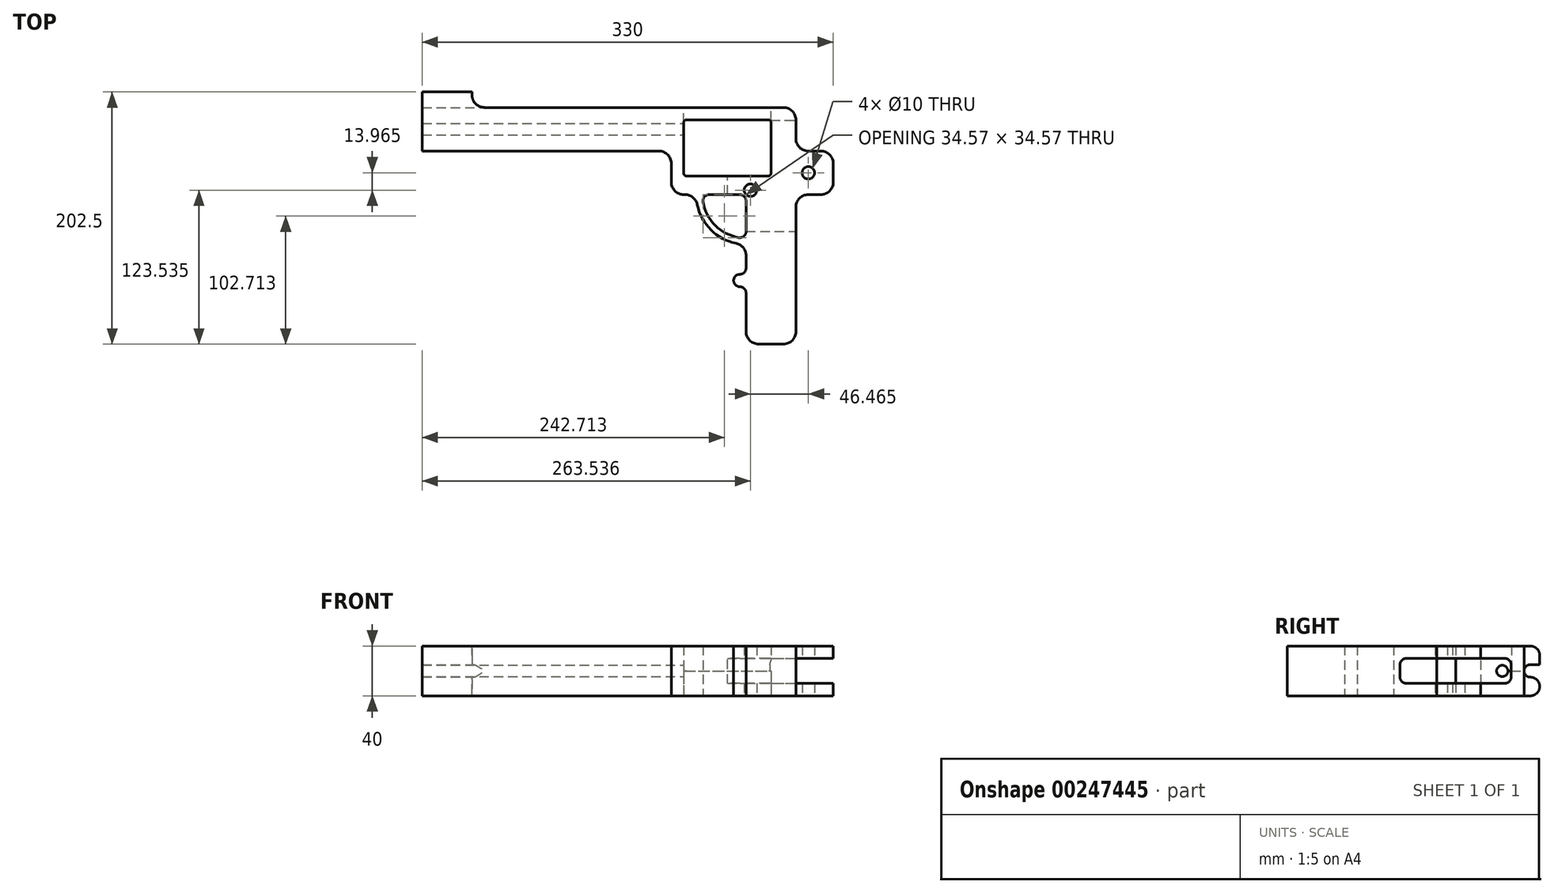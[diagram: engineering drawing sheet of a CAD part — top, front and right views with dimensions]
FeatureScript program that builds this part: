
annotation { "Feature Type Name" : "Feature", "Feature Type Description" : "" }
export const myFeature = defineFeature(function(context is Context, id is Id, definition is map)
    precondition{}
    {
        {
            var Q0;
            Q0=qCreatedBy(makeId("Top.planeOp"),FACE);
            var sketch = newSketch(context, id + "F0", { "sketchPlane" : qUnion([Q0])});
            skLineSegment(sketch, "E0.bottom", {"start": v(-20, 0) * mm, "end": v(20, 0) * mm});
            skLineSegment(sketch, "E0.top", {"start": v(-20, -120) * mm, "end": v(20, -120) * mm});
            skLineSegment(sketch, "E0.left", {"start": v(-20, 0) * mm, "end": v(-20, -120) * mm});
            skLineSegment(sketch, "E0.right", {"start": v(20, 0) * mm, "end": v(20, -120) * mm});
            skLineSegment(sketch, "E1.bottom", {"start": v(-80, 70) * mm, "end": v(20, 70) * mm});
            skLineSegment(sketch, "E1.top", {"start": v(-80, 0) * mm, "end": v(20, 0) * mm});
            skLineSegment(sketch, "E1.left", {"start": v(-80, 70) * mm, "end": v(-80, 0) * mm});
            skLineSegment(sketch, "E1.right", {"start": v(20, 70) * mm, "end": v(20, 0) * mm});
            skLineSegment(sketch, "E2.bottom", {"start": v(-50, 57.5) * mm, "end": v(-10, 57.5) * mm, "construction": true});
            skLineSegment(sketch, "E2.top", {"start": v(-50, 12.5) * mm, "end": v(-10, 12.5) * mm, "construction": true});
            skLineSegment(sketch, "E2.left", {"start": v(-50, 57.5) * mm, "end": v(-50, 12.5) * mm, "construction": true});
            skLineSegment(sketch, "E2.right", {"start": v(-10, 57.5) * mm, "end": v(-10, 12.5) * mm, "construction": true});
            skLineSegment(sketch, "E3", {"start": v(-50, 35) * mm, "end": v(-10, 35) * mm, "construction": true});
            skLineSegment(sketch, "E4", {"start": v(-80, 35) * mm, "end": v(20, 35) * mm, "construction": true});
            skLineSegment(sketch, "E5", {"start": v(-30, 70) * mm, "end": v(-30, 35) * mm, "construction": true});
            skLineSegment(sketch, "E6.bottom", {"start": v(20, 35) * mm, "end": v(50, 35) * mm});
            skLineSegment(sketch, "E6.top", {"start": v(20, 0) * mm, "end": v(50, 0) * mm});
            skLineSegment(sketch, "E6.left", {"start": v(20, 35) * mm, "end": v(20, 0) * mm});
            skLineSegment(sketch, "E6.right", {"start": v(50, 35) * mm, "end": v(50, 0) * mm});
            skLineSegment(sketch, "E7.bottom", {"start": v(-280, 70) * mm, "end": v(-80, 70) * mm});
            skLineSegment(sketch, "E7.top", {"start": v(-280, 35) * mm, "end": v(-80, 35) * mm});
            skLineSegment(sketch, "E7.left", {"start": v(-280, 70) * mm, "end": v(-280, 35) * mm});
            skLineSegment(sketch, "E7.right", {"start": v(-80, 70) * mm, "end": v(-80, 35) * mm});
            skArc(sketch, "E8", {"start": v(-60, 0) * mm, "mid": v(-48.28, -28.28) * mm, "end": v(-20, -40) * mm});
            skLineSegment(sketch, "E9.bottom", {"start": v(-280, 82.5) * mm, "end": v(-240, 82.5) * mm});
            skLineSegment(sketch, "E9.top", {"start": v(-280, 70) * mm, "end": v(-240, 70) * mm});
            skLineSegment(sketch, "E9.left", {"start": v(-280, 82.5) * mm, "end": v(-280, 70) * mm});
            skLineSegment(sketch, "E9.right", {"start": v(-240, 82.5) * mm, "end": v(-240, 70) * mm});
            skSolve(sketch);
        }
        {
            var Q0;
            Q0 = qSketchRegion(id + "F0", true);
            extrude(context, id + "F1", {"entities" : qUnion([Q0]), "endBound" : BoundingType.SYMMETRIC, "depth" : 40 * mm});
        }
        {
            var Q0;
            Q0=makeQuery(id+"F1.opExtrude","SWEPT_FACE",FACE,{"disambiguationData":[OSD([sQuery(id+"F0.wireOp",EDGE,"E1.right")])]});
            var sketch = newSketch(context, id + "F2", { "sketchPlane" : qUnion([Q0])});
            skLineSegment(sketch, "E10", {"start": v(35, 20) * mm, "end": v(70, -20) * mm, "construction": true});
            skCircle(sketch, "E11", {"center": v(52.5, 0) * mm, "radius": 4.55 * mm});
            skSolve(sketch);
        }
        {
            var Q0;
            Q0=makeQuery(id+"F2.imprint","IMPRINT",FACE,{"disambiguationData":[TD([[makeQuery(id+"F2.imprint","IMPRINT",EDGE,{"derivedFrom":sQuery(id+"F2.wireOp",EDGE,"E11")}),1.0]])]});
            extrude(context, id + "F3", {"entities" : qUnion([Q0]), "operationType" : NewBodyOperationType.REMOVE, "endBound" : BoundingType.THROUGH_ALL, "oppositeDirection" : true, "depth" : 25 * mm});
        }
        {
            var Q0;
            Q0=makeQuery(id+"F1.opExtrude","SWEPT_FACE",FACE,{"disambiguationData":[OSD([sQuery(id+"F0.wireOp",EDGE,"E9.right")])]});
            var sketch = newSketch(context, id + "F4", { "sketchPlane" : qUnion([Q0])});
            skLineSegment(sketch, "E12.bottom", {"start": v(70, 5) * mm, "end": v(82.5, 5) * mm});
            skLineSegment(sketch, "E12.top", {"start": v(70, -5) * mm, "end": v(82.5, -5) * mm});
            skLineSegment(sketch, "E12.left", {"start": v(70, 5) * mm, "end": v(70, -5) * mm});
            skLineSegment(sketch, "E12.right", {"start": v(82.5, 5) * mm, "end": v(82.5, -5) * mm});
            skLineSegment(sketch, "E13", {"start": v(70, 0) * mm, "end": v(82.5, 0) * mm, "construction": true});
            skSolve(sketch);
        }
        {
            var Q0;
            Q0=makeQuery(id+"F4.imprint","IMPRINT",FACE,{"disambiguationData":[TD([[makeQuery(id+"F4.imprint","IMPRINT",EDGE,{"derivedFrom":sQuery(id+"F4.wireOp",EDGE,"E12.bottom")}),-1.0]])]});
            extrude(context, id + "F5", {"entities" : qUnion([Q0]), "operationType" : NewBodyOperationType.REMOVE, "endBound" : BoundingType.THROUGH_ALL, "oppositeDirection" : true, "depth" : 25 * mm});
        }
        {
            var Q0;
            Q0=makeQuery(id+"F1.opExtrude","SWEPT_EDGE",EDGE,{"disambiguationData":[OSD([sQuery(id+"F0.wireOp",EDGE,"E1.top"),sQuery(id+"F0.wireOp",EDGE,"E8")])]});
            var Q1;
            Q1=makeQuery(id+"F1.opExtrude","SWEPT_EDGE",EDGE,{"disambiguationData":[OSD([sQuery(id+"F0.wireOp",EDGE,"E0.left"),sQuery(id+"F0.wireOp",EDGE,"E8")])]});
            var Q2;
            Q2=makeQuery(id+"F1.opExtrude","SWEPT_EDGE",EDGE,{"disambiguationData":[OSD([sQuery(id+"F0.wireOp",EDGE,"E1.top"),sQuery(id+"F0.wireOp",EDGE,"E1.left")])]});
            var Q3;
            Q3=makeQuery(id+"F1.opExtrude","SWEPT_EDGE",EDGE,{"disambiguationData":[OSD([sQuery(id+"F0.wireOp",EDGE,"E1.left"),sQuery(id+"F0.wireOp",EDGE,"E7.top"),sQuery(id+"F0.wireOp",EDGE,"E7.right")])]});
            var Q4;
            Q4=makeQuery(id+"F1.opExtrude","SWEPT_EDGE",EDGE,{"disambiguationData":[OSD([sQuery(id+"F0.wireOp",EDGE,"E0.right"),sQuery(id+"F0.wireOp",EDGE,"E1.top"),sQuery(id+"F0.wireOp",EDGE,"E6.top"),sQuery(id+"F0.wireOp",EDGE,"E6.left")])]});
            var Q5;
            Q5=makeQuery(id+"F1.opExtrude","SWEPT_EDGE",EDGE,{"disambiguationData":[OSD([sQuery(id+"F0.wireOp",EDGE,"E1.right"),sQuery(id+"F0.wireOp",EDGE,"E6.bottom"),sQuery(id+"F0.wireOp",EDGE,"E6.left")])]});
            var Q6;
            Q6=makeQuery(id+"F1.opExtrude","SWEPT_EDGE",EDGE,{"disambiguationData":[OSD([sQuery(id+"F0.wireOp",EDGE,"E6.bottom"),sQuery(id+"F0.wireOp",EDGE,"E6.right")])]});
            var Q7;
            Q7=makeQuery(id+"F1.opExtrude","SWEPT_EDGE",EDGE,{"disambiguationData":[OSD([sQuery(id+"F0.wireOp",EDGE,"E6.top"),sQuery(id+"F0.wireOp",EDGE,"E6.right")])]});
            var Q8;
            Q8=makeQuery(id+"F1.opExtrude","SWEPT_EDGE",EDGE,{"disambiguationData":[OSD([sQuery(id+"F0.wireOp",EDGE,"E1.bottom"),sQuery(id+"F0.wireOp",EDGE,"E1.right")])]});
            var Q9;
            Q9=makeQuery(id+"F1.opExtrude","SWEPT_EDGE",EDGE,{"disambiguationData":[OSD([sQuery(id+"F0.wireOp",EDGE,"E0.top"),sQuery(id+"F0.wireOp",EDGE,"E0.right")])]});
            var Q10;
            Q10=makeQuery(id+"F1.opExtrude","SWEPT_EDGE",EDGE,{"disambiguationData":[OSD([sQuery(id+"F0.wireOp",EDGE,"E0.top"),sQuery(id+"F0.wireOp",EDGE,"E0.left")])]});
            var Q11;
            {var subQ0=sQuery(id+"F0.wireOp",EDGE,"E9.right");var subQ1=sQuery(id+"F0.wireOp",EDGE,"E7.bottom");Q11=makeQuery(id+"F5.boolean.opBoolean","SPLIT",EDGE,{"disambiguationData":[TD([makeQuery(id+"F5.opExtrude","SWEPT_FACE",FACE,{"disambiguationData":[OSD([sQuery(id+"F4.wireOp",EDGE,"E12.bottom")])]})])],"derivedFrom":makeQuery(id+"F1.opExtrude","SWEPT_EDGE",EDGE,{"disambiguationData":[OSD([subQ1,sQuery(id+"F0.wireOp",EDGE,"E9.top"),subQ0])]})});}
            var Q12;
            {var subQ0=sQuery(id+"F0.wireOp",EDGE,"E7.bottom");var subQ2=sQuery(id+"F0.wireOp",EDGE,"E9.right");Q12=makeQuery(id+"F5.boolean.opBoolean","SPLIT",EDGE,{"disambiguationData":[TD([makeQuery(id+"F5.opExtrude","SWEPT_FACE",FACE,{"disambiguationData":[OSD([sQuery(id+"F4.wireOp",EDGE,"E12.top")])]})])],"derivedFrom":makeQuery(id+"F1.opExtrude","SWEPT_EDGE",EDGE,{"disambiguationData":[OSD([subQ0,sQuery(id+"F0.wireOp",EDGE,"E9.top"),subQ2])]})});}
            fillet(context, id + "F6", {"entities" : qUnion([Q0, Q1, Q2, Q3, Q4, Q5, Q6, Q7, Q8, Q9, Q10, Q11, Q12]), "radius" : 10 * mm, "tangentPropagation" : true, "allowEdgeOverflow" : false});
        }
        {
            var Q0;
            Q0=makeQuery(id+"F1.opExtrude","CAP_FACE",FACE,{"disambiguationData":[OSD([sQuery(id+"F0.wireOp",EDGE,"E0.top"),sQuery(id+"F0.wireOp",EDGE,"E0.left"),sQuery(id+"F0.wireOp",EDGE,"E0.right"),sQuery(id+"F0.wireOp",EDGE,"E1.bottom"),sQuery(id+"F0.wireOp",EDGE,"E1.top"),sQuery(id+"F0.wireOp",EDGE,"E1.left"),sQuery(id+"F0.wireOp",EDGE,"E1.right"),sQuery(id+"F0.wireOp",EDGE,"E6.bottom"),sQuery(id+"F0.wireOp",EDGE,"E6.top"),sQuery(id+"F0.wireOp",EDGE,"E6.right"),sQuery(id+"F0.wireOp",EDGE,"E7.bottom"),sQuery(id+"F0.wireOp",EDGE,"E7.top"),sQuery(id+"F0.wireOp",EDGE,"E7.left"),sQuery(id+"F0.wireOp",EDGE,"E8"),sQuery(id+"F0.wireOp",EDGE,"E9.bottom"),sQuery(id+"F0.wireOp",EDGE,"E9.left"),sQuery(id+"F0.wireOp",EDGE,"E9.right")])],"isStart":true});
            var sketch = newSketch(context, id + "F7", { "sketchPlane" : qUnion([Q0])});
            skCircle(sketch, "E14", {"center": v(-20, 0) * mm, "radius": 35 * mm, "construction": true});
            skLineSegment(sketch, "E15", {"start": v(-20, 35) * mm, "end": v(-20, 0) * mm});
            skLineSegment(sketch, "E16", {"start": v(-20, 0) * mm, "end": v(-55, 0) * mm});
            skArc(sketch, "E17", {"start": v(-20, 35) * mm, "mid": v(-44.75, 24.75) * mm, "end": v(-55, 0) * mm});
            skSolve(sketch);
        }
        {
            var Q0;
            Q0=makeQuery(id+"F7.imprint","IMPRINT",FACE,{"disambiguationData":[TD([[makeQuery(id+"F7.imprint","IMPRINT",EDGE,{"derivedFrom":sQuery(id+"F7.wireOp",EDGE,"E15")}),-1.0]])]});
            extrude(context, id + "F8", {"entities" : qUnion([Q0]), "operationType" : NewBodyOperationType.REMOVE, "endBound" : BoundingType.THROUGH_ALL, "oppositeDirection" : true, "depth" : 25 * mm});
        }
        {
            var Q0;
            Q0=makeQuery(id+"F8.boolean.opBoolean","COPY",EDGE,{"derivedFrom":makeQuery(id+"F8.opExtrude","SWEPT_EDGE",EDGE,{"disambiguationData":[OSD([sQuery(id+"F7.wireOp",EDGE,"E16"),sQuery(id+"F7.wireOp",EDGE,"E17")])]})});
            var Q1;
            Q1=makeQuery(id+"F8.boolean.opBoolean","COPY",EDGE,{"derivedFrom":makeQuery(id+"F8.opExtrude","SWEPT_EDGE",EDGE,{"disambiguationData":[OSD([sQuery(id+"F7.wireOp",EDGE,"E15"),sQuery(id+"F7.wireOp",EDGE,"E17")])]})});
            var Q2;
            Q2=makeQuery(id+"F8.boolean.opBoolean","COPY",EDGE,{"derivedFrom":makeQuery(id+"F8.opExtrude","SWEPT_EDGE",EDGE,{"disambiguationData":[OSD([sQuery(id+"F7.wireOp",EDGE,"E15"),sQuery(id+"F7.wireOp",EDGE,"E16")])]})});
            fillet(context, id + "F9", {"entities" : qUnion([Q0, Q1, Q2]), "radius" : 5 * mm, "tangentPropagation" : true, "allowEdgeOverflow" : false});
        }
        {
            var Q0;
            Q0=makeQuery(id+"F1.opExtrude","CAP_FACE",FACE,{"disambiguationData":[OSD([sQuery(id+"F0.wireOp",EDGE,"E0.top"),sQuery(id+"F0.wireOp",EDGE,"E0.left"),sQuery(id+"F0.wireOp",EDGE,"E0.right"),sQuery(id+"F0.wireOp",EDGE,"E1.bottom"),sQuery(id+"F0.wireOp",EDGE,"E1.top"),sQuery(id+"F0.wireOp",EDGE,"E1.left"),sQuery(id+"F0.wireOp",EDGE,"E1.right"),sQuery(id+"F0.wireOp",EDGE,"E6.bottom"),sQuery(id+"F0.wireOp",EDGE,"E6.top"),sQuery(id+"F0.wireOp",EDGE,"E6.right"),sQuery(id+"F0.wireOp",EDGE,"E7.bottom"),sQuery(id+"F0.wireOp",EDGE,"E7.top"),sQuery(id+"F0.wireOp",EDGE,"E7.left"),sQuery(id+"F0.wireOp",EDGE,"E8"),sQuery(id+"F0.wireOp",EDGE,"E9.bottom"),sQuery(id+"F0.wireOp",EDGE,"E9.left"),sQuery(id+"F0.wireOp",EDGE,"E9.right")])],"isStart":true});
            var sketch = newSketch(context, id + "F10", { "sketchPlane" : qUnion([Q0])});
            skCircle(sketch, "E18", {"center": v(-25, 58.99) * mm, "radius": 5 * mm, "construction": true});
            skCircle(sketch, "E19.0.1.0", {"center": v(-25, 68.99) * mm, "radius": 5 * mm, "construction": true});
            skCircle(sketch, "E19.0.2.0", {"center": v(-25, 78.99) * mm, "radius": 5 * mm, "construction": true});
            skLineSegment(sketch, "E19.direction1", {"start": v(-25, 58.99) * mm, "end": v(-20, 58.99) * mm, "construction": true});
            skLineSegment(sketch, "E19.direction2", {"start": v(-25, 58.99) * mm, "end": v(-25, 68.99) * mm, "construction": true});
            skArc(sketch, "E20", {"start": v(-20, 58.99) * mm, "mid": v(-21.46, 62.53) * mm, "end": v(-25, 63.99) * mm});
            skArc(sketch, "E21", {"start": v(-25, 73.99) * mm, "mid": v(-30, 68.99) * mm, "end": v(-25, 63.99) * mm});
            skArc(sketch, "E22", {"start": v(-25, 73.99) * mm, "mid": v(-21.46, 75.45) * mm, "end": v(-20, 78.99) * mm});
            skSolve(sketch);
        }
        {
            var Q0;
            {var subQ0=sQuery(id+"F10.wireOp",EDGE,"E20");Q0=makeQuery(id+"F10.imprint","IMPRINT",FACE,{"disambiguationData":[TD([[makeQuery(id+"F10.imprint","IMPRINT",EDGE,{"derivedFrom":subQ0}),-1.0]])]});}
            var Q1;
            Q1=makeQuery(id+"F1.opExtrude","CAP_FACE",FACE,{"disambiguationData":[OSD([sQuery(id+"F0.wireOp",EDGE,"E0.top"),sQuery(id+"F0.wireOp",EDGE,"E0.left"),sQuery(id+"F0.wireOp",EDGE,"E0.right"),sQuery(id+"F0.wireOp",EDGE,"E1.bottom"),sQuery(id+"F0.wireOp",EDGE,"E1.top"),sQuery(id+"F0.wireOp",EDGE,"E1.left"),sQuery(id+"F0.wireOp",EDGE,"E1.right"),sQuery(id+"F0.wireOp",EDGE,"E6.bottom"),sQuery(id+"F0.wireOp",EDGE,"E6.top"),sQuery(id+"F0.wireOp",EDGE,"E6.right"),sQuery(id+"F0.wireOp",EDGE,"E7.bottom"),sQuery(id+"F0.wireOp",EDGE,"E7.top"),sQuery(id+"F0.wireOp",EDGE,"E7.left"),sQuery(id+"F0.wireOp",EDGE,"E8"),sQuery(id+"F0.wireOp",EDGE,"E9.bottom"),sQuery(id+"F0.wireOp",EDGE,"E9.left"),sQuery(id+"F0.wireOp",EDGE,"E9.right")])],"isStart":false});
            extrude(context, id + "F11", {"entities" : qUnion([Q0]), "operationType" : NewBodyOperationType.ADD, "endBound" : BoundingType.UP_TO_SURFACE, "oppositeDirection" : true, "endBoundEntityFace" : qUnion([Q1]), "depth" : 25 * mm});
        }
        {
            var Q0;
            Q0=makeQuery(id+"F5.boolean.opBoolean","MERGE",FACE,{"derivedFrom":[makeQuery(id+"F1.opExtrude","SWEPT_FACE",FACE,{"disambiguationData":[OSD([sQuery(id+"F0.wireOp",EDGE,"E1.bottom"),sQuery(id+"F0.wireOp",EDGE,"E7.bottom")])]}),makeQuery(id+"F5.opExtrude","SWEPT_FACE",FACE,{"disambiguationData":[OSD([sQuery(id+"F4.wireOp",EDGE,"E12.left")])]})]});
            var sketch = newSketch(context, id + "F12", { "sketchPlane" : qUnion([Q0])});
            skLineSegment(sketch, "E23.bottom", {"start": v(-70, 10) * mm, "end": v(-20, 10) * mm});
            skLineSegment(sketch, "E23.top", {"start": v(-70, -10) * mm, "end": v(-20, -10) * mm});
            skLineSegment(sketch, "E23.left", {"start": v(-70, 10) * mm, "end": v(-70, -10) * mm});
            skLineSegment(sketch, "E23.right", {"start": v(-20, 10) * mm, "end": v(-20, -10) * mm});
            skLineSegment(sketch, "E24", {"start": v(-70, 0) * mm, "end": v(-20, 0) * mm, "construction": true});
            skSolve(sketch);
        }
        {
            var Q0;
            Q0=makeQuery(id+"F12.imprint","IMPRINT",FACE,{"disambiguationData":[TD([[makeQuery(id+"F12.imprint","IMPRINT",EDGE,{"derivedFrom":sQuery(id+"F12.wireOp",EDGE,"E23.bottom")}),-1.0]])]});
            extrude(context, id + "F13", {"entities" : qUnion([Q0]), "operationType" : NewBodyOperationType.REMOVE, "endBound" : BoundingType.THROUGH_ALL, "oppositeDirection" : true, "depth" : 25 * mm});
        }
        {
            var Q0;
            {var subQ0=sQuery(id+"F0.wireOp",EDGE,"E0.left");Q0=makeQuery(id+"F11.boolean.opBoolean","MERGE",FACE,{"derivedFrom":[makeQuery(id+"F1.opExtrude","CAP_FACE",FACE,{"disambiguationData":[OSD([sQuery(id+"F0.wireOp",EDGE,"E0.top"),subQ0,sQuery(id+"F0.wireOp",EDGE,"E0.right"),sQuery(id+"F0.wireOp",EDGE,"E1.bottom"),sQuery(id+"F0.wireOp",EDGE,"E1.top"),sQuery(id+"F0.wireOp",EDGE,"E1.left"),sQuery(id+"F0.wireOp",EDGE,"E1.right"),sQuery(id+"F0.wireOp",EDGE,"E6.bottom"),sQuery(id+"F0.wireOp",EDGE,"E6.top"),sQuery(id+"F0.wireOp",EDGE,"E6.right"),sQuery(id+"F0.wireOp",EDGE,"E7.bottom"),sQuery(id+"F0.wireOp",EDGE,"E7.top"),sQuery(id+"F0.wireOp",EDGE,"E7.left"),sQuery(id+"F0.wireOp",EDGE,"E8"),sQuery(id+"F0.wireOp",EDGE,"E9.bottom"),sQuery(id+"F0.wireOp",EDGE,"E9.left"),sQuery(id+"F0.wireOp",EDGE,"E9.right")])],"isStart":true}),makeQuery(id+"F11.opExtrude","CAP_FACE",FACE,{"disambiguationData":[OSD([subQ0,sQuery(id+"F10.wireOp",EDGE,"E20"),sQuery(id+"F10.wireOp",EDGE,"E21"),sQuery(id+"F10.wireOp",EDGE,"E22")])],"isStart":true})]});}
            var sketch = newSketch(context, id + "F14", { "sketchPlane" : qUnion([Q0])});
            skLineSegment(sketch, "E25.bottom", {"start": v(-70, -15) * mm, "end": v(0, -15) * mm});
            skLineSegment(sketch, "E25.top", {"start": v(-70, -60) * mm, "end": v(0, -60) * mm});
            skLineSegment(sketch, "E25.left", {"start": v(-70, -15) * mm, "end": v(-70, -60) * mm});
            skLineSegment(sketch, "E25.right", {"start": v(0, -15) * mm, "end": v(0, -60) * mm});
            skSolve(sketch);
        }
        {
            var Q0;
            Q0=makeQuery(id+"F14.imprint","IMPRINT",FACE,{"disambiguationData":[TD([[makeQuery(id+"F14.imprint","IMPRINT",EDGE,{"derivedFrom":sQuery(id+"F14.wireOp",EDGE,"E25.bottom")}),-1.0]])]});
            extrude(context, id + "F15", {"entities" : qUnion([Q0]), "operationType" : NewBodyOperationType.REMOVE, "endBound" : BoundingType.THROUGH_ALL, "oppositeDirection" : true, "depth" : 25 * mm});
        }
        {
            var Q0;
            Q0=makeQuery(id+"F15.boolean.opBoolean","COPY",EDGE,{"derivedFrom":makeQuery(id+"F15.opExtrude","SWEPT_EDGE",EDGE,{"disambiguationData":[OSD([sQuery(id+"F14.wireOp",EDGE,"E25.top"),sQuery(id+"F14.wireOp",EDGE,"E25.right")])]})});
            var Q1;
            Q1=makeQuery(id+"F15.boolean.opBoolean","COPY",EDGE,{"derivedFrom":makeQuery(id+"F15.opExtrude","SWEPT_EDGE",EDGE,{"disambiguationData":[OSD([sQuery(id+"F14.wireOp",EDGE,"E25.bottom"),sQuery(id+"F14.wireOp",EDGE,"E25.right")])]})});
            var Q2;
            Q2=makeQuery(id+"F15.boolean.opBoolean","COPY",EDGE,{"derivedFrom":makeQuery(id+"F15.opExtrude","SWEPT_EDGE",EDGE,{"disambiguationData":[OSD([sQuery(id+"F14.wireOp",EDGE,"E25.top"),sQuery(id+"F14.wireOp",EDGE,"E25.left")])]})});
            var Q3;
            Q3=makeQuery(id+"F15.boolean.opBoolean","COPY",EDGE,{"derivedFrom":makeQuery(id+"F15.opExtrude","SWEPT_EDGE",EDGE,{"disambiguationData":[OSD([sQuery(id+"F14.wireOp",EDGE,"E25.bottom"),sQuery(id+"F14.wireOp",EDGE,"E25.left")])]})});
            fillet(context, id + "F16", {"entities" : qUnion([Q0, Q1, Q2, Q3]), "radius" : 2 * mm, "tangentPropagation" : true, "allowEdgeOverflow" : false});
        }
        {
            var Q0;
            Q0=makeQuery(id+"F13.boolean.opBoolean","MERGE",FACE,{"derivedFrom":[makeQuery(id+"F1.opExtrude","SWEPT_FACE",FACE,{"disambiguationData":[OSD([sQuery(id+"F0.wireOp",EDGE,"E0.right")])]}),makeQuery(id+"F1.opExtrude","SWEPT_FACE",FACE,{"disambiguationData":[OSD([sQuery(id+"F0.wireOp",EDGE,"E1.right")])]}),makeQuery(id+"F13.opExtrude","SWEPT_FACE",FACE,{"disambiguationData":[OSD([sQuery(id+"F12.wireOp",EDGE,"E23.right")])]})]});
            var sketch = newSketch(context, id + "F17", { "sketchPlane" : qUnion([Q0])});
            skLineSegment(sketch, "E26.bottom", {"start": v(-29.58, 10) * mm, "end": v(15, 10) * mm});
            skLineSegment(sketch, "E26.top", {"start": v(-29.58, -10) * mm, "end": v(15, -10) * mm});
            skLineSegment(sketch, "E26.left", {"start": v(-29.58, 10) * mm, "end": v(-29.58, -10) * mm});
            skLineSegment(sketch, "E26.right", {"start": v(15, 10) * mm, "end": v(15, -10) * mm});
            skLineSegment(sketch, "E27.MirrorCS", {"start": v(59.58, -10) * mm, "end": v(15, -10) * mm});
            skLineSegment(sketch, "E28.MirrorCS", {"start": v(59.58, 10) * mm, "end": v(15, 10) * mm});
            skLineSegment(sketch, "E29.MirrorCS", {"start": v(59.58, 10) * mm, "end": v(59.58, -10) * mm});
            skSolve(sketch);
        }
        {
            var Q0;
            {var subQ28=sQuery(id+"F17.wireOp",EDGE,"E26.right");Q0=makeQuery(id+"F17.imprint","IMPRINT",FACE,{"disambiguationData":[TD([[makeQuery(id+"F17.imprint","IMPRINT",EDGE,{"derivedFrom":subQ28}),1.0]])]});}
            var Q1;
            {var subQ26=sQuery(id+"F17.wireOp",EDGE,"E26.left");Q1=makeQuery(id+"F17.imprint","IMPRINT",FACE,{"disambiguationData":[TD([[makeQuery(id+"F17.imprint","IMPRINT",EDGE,{"derivedFrom":subQ26}),1.0]])]});}
            extrude(context, id + "F18", {"entities" : qUnion([Q0, Q1]), "operationType" : NewBodyOperationType.REMOVE, "oppositeDirection" : true, "depth" : 55 * mm});
        }
        {
            var Q0;
            Q0=makeQuery(id+"F18.boolean.opBoolean","COPY",EDGE,{"derivedFrom":makeQuery(id+"F18.opExtrude","SWEPT_EDGE",EDGE,{"disambiguationData":[OSD([sQuery(id+"F17.wireOp",EDGE,"E26.bottom"),sQuery(id+"F17.wireOp",EDGE,"E26.left")])]})});
            var Q1;
            Q1=makeQuery(id+"F18.boolean.opBoolean","COPY",EDGE,{"derivedFrom":makeQuery(id+"F18.opExtrude","SWEPT_EDGE",EDGE,{"disambiguationData":[OSD([sQuery(id+"F17.wireOp",EDGE,"E26.top"),sQuery(id+"F17.wireOp",EDGE,"E26.left")])]})});
            var Q2;
            Q2=makeQuery(id+"F18.boolean.opBoolean","COPY",EDGE,{"derivedFrom":makeQuery(id+"F18.opExtrude","SWEPT_EDGE",EDGE,{"disambiguationData":[OSD([sQuery(id+"F17.wireOp",EDGE,"E28.MirrorCS"),sQuery(id+"F17.wireOp",EDGE,"E29.MirrorCS")])]})});
            var Q3;
            Q3=makeQuery(id+"F18.boolean.opBoolean","COPY",EDGE,{"derivedFrom":makeQuery(id+"F18.opExtrude","SWEPT_EDGE",EDGE,{"disambiguationData":[OSD([sQuery(id+"F17.wireOp",EDGE,"E27.MirrorCS"),sQuery(id+"F17.wireOp",EDGE,"E29.MirrorCS")])]})});
            fillet(context, id + "F19", {"entities" : qUnion([Q0, Q1, Q2, Q3]), "radius" : 5 * mm, "tangentPropagation" : true, "allowEdgeOverflow" : false});
        }
        {
            var Q0;
            {var subQ0=sQuery(id+"F0.wireOp",EDGE,"E0.left");Q0=makeQuery(id+"F11.boolean.opBoolean","MERGE",FACE,{"derivedFrom":[makeQuery(id+"F1.opExtrude","CAP_FACE",FACE,{"disambiguationData":[OSD([sQuery(id+"F0.wireOp",EDGE,"E0.top"),subQ0,sQuery(id+"F0.wireOp",EDGE,"E0.right"),sQuery(id+"F0.wireOp",EDGE,"E1.bottom"),sQuery(id+"F0.wireOp",EDGE,"E1.top"),sQuery(id+"F0.wireOp",EDGE,"E1.left"),sQuery(id+"F0.wireOp",EDGE,"E1.right"),sQuery(id+"F0.wireOp",EDGE,"E6.bottom"),sQuery(id+"F0.wireOp",EDGE,"E6.top"),sQuery(id+"F0.wireOp",EDGE,"E6.right"),sQuery(id+"F0.wireOp",EDGE,"E7.bottom"),sQuery(id+"F0.wireOp",EDGE,"E7.top"),sQuery(id+"F0.wireOp",EDGE,"E7.left"),sQuery(id+"F0.wireOp",EDGE,"E8"),sQuery(id+"F0.wireOp",EDGE,"E9.bottom"),sQuery(id+"F0.wireOp",EDGE,"E9.left"),sQuery(id+"F0.wireOp",EDGE,"E9.right")])],"isStart":true}),makeQuery(id+"F11.opExtrude","CAP_FACE",FACE,{"disambiguationData":[OSD([subQ0,sQuery(id+"F10.wireOp",EDGE,"E20"),sQuery(id+"F10.wireOp",EDGE,"E21"),sQuery(id+"F10.wireOp",EDGE,"E22")])],"isStart":true})]});}
            var sketch = newSketch(context, id + "F20", { "sketchPlane" : qUnion([Q0])});
            skCircle(sketch, "E30", {"center": v(30, -17.5) * mm, "radius": 5 * mm});
            skLineSegment(sketch, "E31", {"start": v(30, -17.5) * mm, "end": v(50, -17.5) * mm, "construction": true});
            skSolve(sketch);
        }
        {
            var Q0;
            Q0=makeQuery(id+"F20.imprint","IMPRINT",FACE,{"disambiguationData":[TD([[makeQuery(id+"F20.imprint","IMPRINT",EDGE,{"derivedFrom":sQuery(id+"F20.wireOp",EDGE,"E30")}),1.0]])]});
            extrude(context, id + "F21", {"entities" : qUnion([Q0]), "operationType" : NewBodyOperationType.REMOVE, "endBound" : BoundingType.THROUGH_ALL, "oppositeDirection" : true, "depth" : 63 * mm});
        }
        {
            var Q0;
            {var subQ0=sQuery(id+"F0.wireOp",EDGE,"E0.left");Q0=makeQuery(id+"F11.boolean.opBoolean","MERGE",FACE,{"derivedFrom":[makeQuery(id+"F1.opExtrude","CAP_FACE",FACE,{"disambiguationData":[OSD([sQuery(id+"F0.wireOp",EDGE,"E0.top"),subQ0,sQuery(id+"F0.wireOp",EDGE,"E0.right"),sQuery(id+"F0.wireOp",EDGE,"E1.bottom"),sQuery(id+"F0.wireOp",EDGE,"E1.top"),sQuery(id+"F0.wireOp",EDGE,"E1.left"),sQuery(id+"F0.wireOp",EDGE,"E1.right"),sQuery(id+"F0.wireOp",EDGE,"E6.bottom"),sQuery(id+"F0.wireOp",EDGE,"E6.top"),sQuery(id+"F0.wireOp",EDGE,"E6.right"),sQuery(id+"F0.wireOp",EDGE,"E7.bottom"),sQuery(id+"F0.wireOp",EDGE,"E7.top"),sQuery(id+"F0.wireOp",EDGE,"E7.left"),sQuery(id+"F0.wireOp",EDGE,"E8"),sQuery(id+"F0.wireOp",EDGE,"E9.bottom"),sQuery(id+"F0.wireOp",EDGE,"E9.left"),sQuery(id+"F0.wireOp",EDGE,"E9.right")])],"isStart":true}),makeQuery(id+"F11.opExtrude","CAP_FACE",FACE,{"disambiguationData":[OSD([subQ0,sQuery(id+"F10.wireOp",EDGE,"E20"),sQuery(id+"F10.wireOp",EDGE,"E21"),sQuery(id+"F10.wireOp",EDGE,"E22")])],"isStart":true})]});}
            var sketch = newSketch(context, id + "F22", { "sketchPlane" : qUnion([Q0])});
            skCircle(sketch, "E32", {"center": v(-16.46, -3.54) * mm, "radius": 5 * mm});
            skLineSegment(sketch, "E33", {"start": v(-44.75, 24.75) * mm, "end": v(-16.46, -3.54) * mm, "construction": true});
            skSolve(sketch);
        }
        {
            var Q0;
            Q0=makeQuery(id+"F22.imprint","IMPRINT",FACE,{"disambiguationData":[TD([[makeQuery(id+"F22.imprint","IMPRINT",EDGE,{"derivedFrom":sQuery(id+"F22.wireOp",EDGE,"E32")}),1.0]])]});
            extrude(context, id + "F23", {"entities" : qUnion([Q0]), "operationType" : NewBodyOperationType.REMOVE, "endBound" : BoundingType.THROUGH_ALL, "oppositeDirection" : true, "depth" : 25 * mm});
        }
        {
            var Q0;
            {var subQ0=sQuery(id+"F0.wireOp",EDGE,"E0.left");Q0=makeQuery(id+"F11.boolean.opBoolean","MERGE",FACE,{"derivedFrom":[makeQuery(id+"F1.opExtrude","CAP_FACE",FACE,{"disambiguationData":[OSD([sQuery(id+"F0.wireOp",EDGE,"E0.top"),subQ0,sQuery(id+"F0.wireOp",EDGE,"E0.right"),sQuery(id+"F0.wireOp",EDGE,"E1.bottom"),sQuery(id+"F0.wireOp",EDGE,"E1.top"),sQuery(id+"F0.wireOp",EDGE,"E1.left"),sQuery(id+"F0.wireOp",EDGE,"E1.right"),sQuery(id+"F0.wireOp",EDGE,"E6.bottom"),sQuery(id+"F0.wireOp",EDGE,"E6.top"),sQuery(id+"F0.wireOp",EDGE,"E6.right"),sQuery(id+"F0.wireOp",EDGE,"E7.bottom"),sQuery(id+"F0.wireOp",EDGE,"E7.top"),sQuery(id+"F0.wireOp",EDGE,"E7.left"),sQuery(id+"F0.wireOp",EDGE,"E8"),sQuery(id+"F0.wireOp",EDGE,"E9.bottom"),sQuery(id+"F0.wireOp",EDGE,"E9.left"),sQuery(id+"F0.wireOp",EDGE,"E9.right")])],"isStart":true}),makeQuery(id+"F11.opExtrude","CAP_FACE",FACE,{"disambiguationData":[OSD([subQ0,sQuery(id+"F10.wireOp",EDGE,"E20"),sQuery(id+"F10.wireOp",EDGE,"E21"),sQuery(id+"F10.wireOp",EDGE,"E22")])],"isStart":true})]});}
            var sketch = newSketch(context, id + "F24", { "sketchPlane" : qUnion([Q0])});
            skLineSegment(sketch, "E34.bottom", {"start": v(-70, -17) * mm, "end": v(0, -17) * mm});
            skLineSegment(sketch, "E34.top", {"start": v(-70, -70) * mm, "end": v(0, -70) * mm});
            skLineSegment(sketch, "E34.left", {"start": v(-70, -17) * mm, "end": v(-70, -70) * mm});
            skLineSegment(sketch, "E34.right", {"start": v(0, -17) * mm, "end": v(0, -70) * mm});
            skSolve(sketch);
        }
        {
            var Q0;
            {var subQ8=sQuery(id+"F24.wireOp",EDGE,"E34.top");Q0=makeQuery(id+"F24.imprint","IMPRINT",FACE,{"disambiguationData":[TD([[makeQuery(id+"F24.imprint","IMPRINT",EDGE,{"derivedFrom":subQ8}),1.0]])]});}
            var Q1;
            Q1=qCreatedBy(makeId("Top.planeOp"),FACE);
            extrude(context, id + "F25", {"entities" : qUnion([Q0]), "operationType" : NewBodyOperationType.REMOVE, "endBound" : BoundingType.UP_TO_SURFACE, "oppositeDirection" : true, "endBoundEntityFace" : qUnion([Q1]), "depth" : 25 * mm});
        }
        {
            var Q0;
            Q0=makeQuery(id+"F5.boolean.opBoolean","COPY",EDGE,{"derivedFrom":makeQuery(id+"F5.opExtrude","SWEPT_EDGE",EDGE,{"disambiguationData":[OSD([sQuery(id+"F0.wireOp",EDGE,"E7.bottom"),sQuery(id+"F0.wireOp",EDGE,"E9.top"),sQuery(id+"F0.wireOp",EDGE,"E9.right"),sQuery(id+"F4.wireOp",EDGE,"E12.top"),sQuery(id+"F4.wireOp",EDGE,"E12.left")])]})});
            var Q1;
            Q1=makeQuery(id+"F5.boolean.opBoolean","COPY",EDGE,{"derivedFrom":makeQuery(id+"F5.opExtrude","SWEPT_EDGE",EDGE,{"disambiguationData":[OSD([sQuery(id+"F0.wireOp",EDGE,"E7.bottom"),sQuery(id+"F0.wireOp",EDGE,"E9.top"),sQuery(id+"F0.wireOp",EDGE,"E9.right"),sQuery(id+"F4.wireOp",EDGE,"E12.bottom"),sQuery(id+"F4.wireOp",EDGE,"E12.left")])]})});
            fillet(context, id + "F26", {"entities" : qUnion([Q0, Q1]), "radius" : 5 * mm, "tangentPropagation" : true, "allowEdgeOverflow" : false});
        }
        {
            var Q0;
            Q0=makeQuery(id+"F5.boolean.opBoolean","COPY",EDGE,{"derivedFrom":makeQuery(id+"F5.opExtrude","SWEPT_EDGE",EDGE,{"disambiguationData":[OSD([sQuery(id+"F0.wireOp",EDGE,"E9.bottom"),sQuery(id+"F0.wireOp",EDGE,"E9.right"),sQuery(id+"F4.wireOp",EDGE,"E12.top"),sQuery(id+"F4.wireOp",EDGE,"E12.right")])]})});
            var Q1;
            Q1=makeQuery(id+"F1.opExtrude","CAP_EDGE",EDGE,{"disambiguationData":[OSD([sQuery(id+"F0.wireOp",EDGE,"E9.bottom")])],"isStart":true});
            var Q2;
            Q2=makeQuery(id+"F5.boolean.opBoolean","COPY",EDGE,{"derivedFrom":makeQuery(id+"F5.opExtrude","SWEPT_EDGE",EDGE,{"disambiguationData":[OSD([sQuery(id+"F0.wireOp",EDGE,"E9.bottom"),sQuery(id+"F0.wireOp",EDGE,"E9.right"),sQuery(id+"F4.wireOp",EDGE,"E12.bottom"),sQuery(id+"F4.wireOp",EDGE,"E12.right")])]})});
            var Q3;
            Q3=makeQuery(id+"F1.opExtrude","CAP_EDGE",EDGE,{"disambiguationData":[OSD([sQuery(id+"F0.wireOp",EDGE,"E9.bottom")])],"isStart":false});
            fillet(context, id + "F27", {"entities" : qUnion([Q0, Q1, Q2, Q3]), "radius" : 7.5 * mm, "tangentPropagation" : true, "allowEdgeOverflow" : false});
        }
    });
